# Revit family: Axis-Jet-VI
name_source: partatom
category: Оборудование
units: mm (PartAtom-declared; Revit-internal decimal feet)

## family parameters
Всегда вертикально = Да
Классификация = Нет
На основе рабочей плоскости = Нет
Общий = Нет
При загрузке вырезать с полостями = Нет
Размер круглого соединителя = Использовать диаметр
Тип детали = Нормальный
Точка принадлежности помещению = Нет

## types (54) — shared parameters
Air Flow = 0.0 м³/ч
Thrust = 0.00 Н
Изготовитель = BLAUBERG
zero-valued in all types: Отметка по умолчанию

## per-type parameters (varying)
| type | H | L | L2 | Maximum Air Flow |
| Axis-Jet-VI-315-2-U-300/2 | 347 мм | 1846 мм | 572 мм | 4500.0 м³/ч |
| Axis-Jet-VI-400-2/4-R-300/2 | 434 мм | 2296 мм | 667 мм | 8300.0 м³/ч |
| Axis-Jet-VI-355M-2-U | 388 мм | 2046 мм | 613 мм | 6750.0 м³/ч |
| Axis-Jet-VI-315-2/4-R-400/2 | 347 мм | 1846 мм | 572 мм | 3000.0 м³/ч |
| Axis-Jet-VI-355-2/4-R-300/2 | 388 мм | 2046 мм | 613 мм | 5800.0 м³/ч |
| Axis-Jet-VI-400-2-U-400/2 | 434 мм | 2296 мм | 667 мм | 7000.0 м³/ч |
| Axis-Jet-VI-315M-2/4-U | 347 мм | 1846 мм | 572 мм | 5000.0 м³/ч |
| Axis-Jet-VI-355-2/4-U-400/2 | 388 мм | 2046 мм | 613 мм | 4900.0 м³/ч |
| Axis-Jet-VI-400-2/4-U-300/2 | 434 мм | 2296 мм | 667 мм | 8500.0 м³/ч |
| Axis-Jet-VI-315-2-U | 347 мм | 1846 мм | 572 мм | 4500.0 м³/ч |
| Axis-Jet-VI-315-2-U-400/2 | 347 мм | 1846 мм | 572 мм | 3250.0 м³/ч |
| Axis-Jet-VI-315M-2-U | 347 мм | 1846 мм | 572 мм | 5000.0 м³/ч |
| Axis-Jet-VI-315M-2-U-300/2 | 347 мм | 1846 мм | 572 мм | 5000.0 м³/ч |
| Axis-Jet-VI-315M-2-U-400/2 | 347 мм | 1846 мм | 572 мм | 3600.0 м³/ч |
| Axis-Jet-VI-315-2/4-U | 347 мм | 1846 мм | 572 мм | 4500.0 м³/ч |
| Axis-Jet-VI-315-2/4-U-300/2 | 347 мм | 1846 мм | 572 мм | 4500.0 м³/ч |
| Axis-Jet-VI-315-2/4-U-400/2 | 347 мм | 1846 мм | 572 мм | 3250.0 м³/ч |
| Axis-Jet-VI-315M-2/4-U-300/2 | 347 мм | 1846 мм | 572 мм | 5000.0 м³/ч |
| Axis-Jet-VI-315M-2/4-U-400/2 | 347 мм | 1846 мм | 572 мм | 3600.0 м³/ч |
| Axis-Jet-VI-315-2-R | 347 мм | 1846 мм | 572 мм | 4200.0 м³/ч |
| Axis-Jet-VI-315-2-R-300/2 | 347 мм | 1846 мм | 572 мм | 4200.0 м³/ч |
| Axis-Jet-VI-315-2-R-400/2 | 347 мм | 1846 мм | 572 мм | 3000.0 м³/ч |
| Axis-Jet-VI-315-2/4-R | 347 мм | 1846 мм | 572 мм | 4200.0 м³/ч |
| Axis-Jet-VI-315-2/4-R-300/2 | 347 мм | 1846 мм | 572 мм | 4200.0 м³/ч |
| Axis-Jet-VI-355-2/4-R | 388 мм | 2046 мм | 613 мм | 5800.0 м³/ч |
| Axis-Jet-VI-355-2-R-300/2 | 388 мм | 2046 мм | 613 мм | 5800.0 м³/ч |
| Axis-Jet-VI-355-2-R | 388 мм | 2046 мм | 613 мм | 5800.0 м³/ч |
| Axis-Jet-VI-355-2-R-400/2 | 388 мм | 2046 мм | 613 мм | 5200.0 м³/ч |
| Axis-Jet-VI-355-2/4-R-400/2 | 388 мм | 2046 мм | 613 мм | 5200.0 м³/ч |
| Axis-Jet-VI-355-2-U | 388 мм | 2046 мм | 613 мм | 5800.0 м³/ч |
| Axis-Jet-VI-355-2-U-300/2 | 388 мм | 2046 мм | 613 мм | 5800.0 м³/ч |
| Axis-Jet-VI-355-2-U-400/2 | 388 мм | 2046 мм | 613 мм | 4900.0 м³/ч |
| Axis-Jet-VI-355M-2-U-300/2 | 388 мм | 2046 мм | 613 мм | 6750.0 м³/ч |
| Axis-Jet-VI-355M-2-U-400/2 | 388 мм | 2046 мм | 613 мм | 5350.0 м³/ч |
| Axis-Jet-VI-355-2/4-U | 388 мм | 2046 мм | 613 мм | 5800.0 м³/ч |
| Axis-Jet-VI-355-2/4-U-300/2 | 388 мм | 2046 мм | 613 мм | 5800.0 м³/ч |
| Axis-Jet-VI-355M-2/4-U | 388 мм | 2046 мм | 613 мм | 6750.0 м³/ч |
| Axis-Jet-VI-355M-2/4-U-300/2 | 388 мм | 2046 мм | 613 мм | 6750.0 м³/ч |
| Axis-Jet-VI-355M-2/4-U-400/2 | 388 мм | 2046 мм | 613 мм | 5350.0 м³/ч |
| Axis-Jet-VI-400-2/4-R | 434 мм | 2296 мм | 667 мм | 8300.0 м³/ч |
| Axis-Jet-VI-400-2-R | 434 мм | 2296 мм | 667 мм | 8300.0 м³/ч |
| Axis-Jet-VI-400-2-R-300/2 | 434 мм | 2296 мм | 667 мм | 8300.0 м³/ч |
| Axis-Jet-VI-400-2-R-400/2 | 434 мм | 2296 мм | 667 мм | 7150.0 м³/ч |
| Axis-Jet-VI-400-2/4-R-400/2 | 434 мм | 2296 мм | 667 мм | 7150.0 м³/ч |
| Axis-Jet-VI-400-2-U | 434 мм | 2296 мм | 667 мм | 8500.0 м³/ч |
| Axis-Jet-VI-400-2-U-300/2 | 434 мм | 2296 мм | 667 мм | 8500.0 м³/ч |
| Axis-Jet-VI-400M-2-U-400/2 | 434 мм | 2296 мм | 667 мм | 8500.0 м³/ч |
| Axis-Jet-VI-400-2/4-U | 434 мм | 2296 мм | 667 мм | 8500.0 м³/ч |
| Axis-Jet-VI-400M-2/4-U-400/2 | 434 мм | 2296 мм | 667 мм | 8500.0 м³/ч |
| Axis-Jet-VI-400-2/4-U-400/2 | 434 мм | 2296 мм | 667 мм | 7000.0 м³/ч |
| Axis-Jet-VI-400M-2-U | 434 мм | 2296 мм | 667 мм | 9850.0 м³/ч |
| Axis-Jet-VI-400M-2-U-300/2 | 434 мм | 2296 мм | 667 мм | 9850.0 м³/ч |
| Axis-Jet-VI-400M-2/4-U | 434 мм | 2296 мм | 667 мм | 9850.0 м³/ч |
| Axis-Jet-VI-400M-2/4-U-300/2 | 434 мм | 2296 мм | 667 мм | 9850.0 м³/ч |
